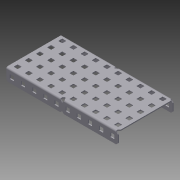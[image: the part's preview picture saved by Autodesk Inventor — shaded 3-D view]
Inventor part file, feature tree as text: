
AUTODESK INVENTOR PART (.ipt)
format: ipt  version: 2014 (Build 180170000, 170)  size: 1,221,632 bytes
history: native  units: in
note: dims shown in document units (in); Inventor stores cm internally (conversion verified against a paired STEP export)
features: other x1, imported_body x1, extrude x1, sketch x1
ambient origin geometry x8: Origin, YZ Plane, XZ Plane, XY Plane, X Axis, Y Axis, Z Axis, Center Point
bodies: Body1 (feature_tree)
feature tree (4):
  parser-record x1  (decoder bookkeeping rows leaked as tree rows — omitted from the tree; the rows remain in map.json)
  imported_body  "Base1"
  extrude  "Extrusion1"  [1 undecoded]
  sketch  "Sketch1"  dims[d0=1.0in d1=0.0in]
note: 1 required parameter value undecoded (feature->parameter linkage not recoverable at this tier; creation-order binding heuristic only, values carry confidence <= 0.55)
